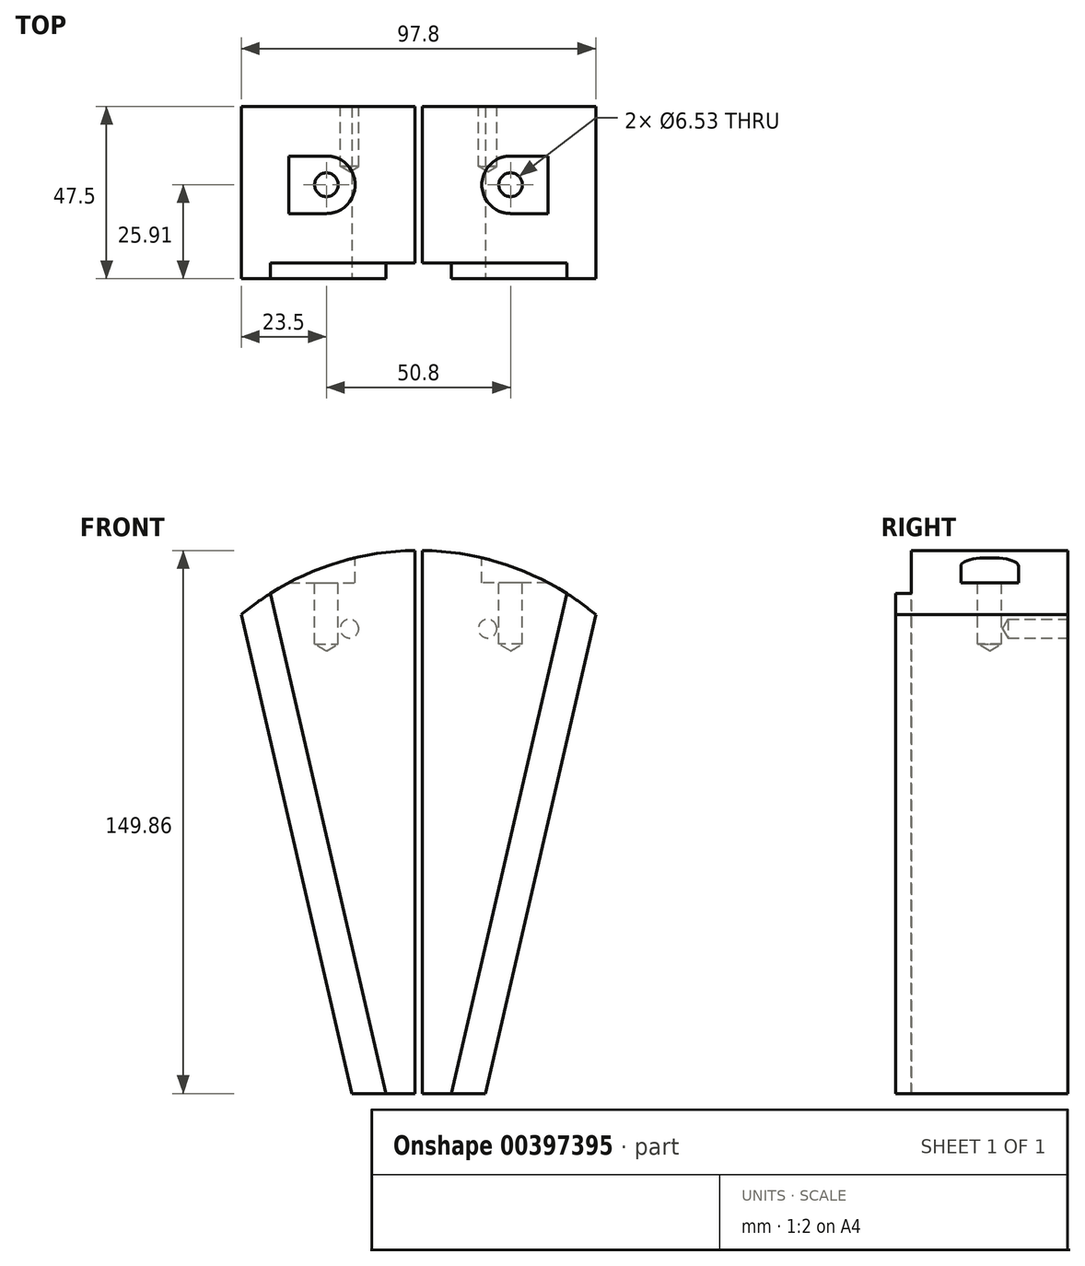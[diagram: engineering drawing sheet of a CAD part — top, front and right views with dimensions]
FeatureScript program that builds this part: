
annotation { "Feature Type Name" : "Feature", "Feature Type Description" : "" }
export const myFeature = defineFeature(function(context is Context, id is Id, definition is map)
    precondition{}
    {
        {
            var Q0;
            Q0=qCreatedBy(makeId("Front.planeOp"),FACE);
            var sketch = newSketch(context, id + "F0", { "sketchPlane" : qUnion([Q0])});
            skLineSegment(sketch, "E0", {"start": v(1.02, 76.2) * mm, "end": v(1.02, -73.67) * mm});
            skLineSegment(sketch, "E1", {"start": v(1.02, -73.67) * mm, "end": v(18.4, -73.67) * mm});
            skLineSegment(sketch, "E2", {"start": v(18.4, -73.67) * mm, "end": v(48.9, 58.44) * mm});
            skLineSegment(sketch, "E3", {"start": v(0, 78.33) * mm, "end": v(0, -85.86) * mm, "construction": true});
            skArc(sketch, "E4", {"start": v(48.9, 58.44) * mm, "mid": v(26, 71.62) * mm, "end": v(0, 76.2) * mm});
            skSolve(sketch);
        }
        {
            var Q0;
            {var subQ0=sQuery(id+"F0.wireOp",EDGE,"E0");Q0=makeQuery(id+"F0.imprint","IMPRINT",FACE,{"disambiguationData":[TD([[makeQuery(id+"F0.imprint","IMPRINT",EDGE,{"derivedFrom":subQ0}),1.0]])]});}
            extrude(context, id + "F1", {"entities" : qUnion([Q0]), "oppositeDirection" : true, "depth" : 21.59 * mm, "offsetDistance" : 25.4 * mm, "hasSecondDirection" : true, "secondDirectionOppositeDirection" : false, "secondDirectionDepth" : 25.9 * mm});
        }
        {
            var Q0;
            Q0=makeQuery(id+"F1.opExtrude","CAP_FACE",FACE,{"disambiguationData":[OSD([sQuery(id+"F0.wireOp",EDGE,"E0"),sQuery(id+"F0.wireOp",EDGE,"E1"),sQuery(id+"F0.wireOp",EDGE,"E2"),sQuery(id+"F0.wireOp",EDGE,"E4")])],"isStart":true});
            var sketch = newSketch(context, id + "F2", { "sketchPlane" : qUnion([Q0])});
            skLineSegment(sketch, "E5", {"start": v(9.01, -73.67) * mm, "end": v(40.87, 64.32) * mm});
            skSolve(sketch);
        }
        {
            var Q0;
            {var subQ0=sQuery(id+"F2.wireOp",EDGE,"E5");Q0=makeQuery(id+"F2.imprint","IMPRINT",FACE,{"disambiguationData":[TD([[makeQuery(id+"F2.imprint","IMPRINT",EDGE,{"derivedFrom":subQ0}),1.0]])]});}
            extrude(context, id + "F3", {"entities" : qUnion([Q0]), "operationType" : NewBodyOperationType.REMOVE, "oppositeDirection" : true, "depth" : 4.32 * mm, "offsetDistance" : 25.4 * mm});
        }
        {
            var Q0;
            Q0=qCreatedBy(makeId("Top.planeOp"),FACE);
            cPlane(context, id + "F4", {"entities" : qUnion([Q0]), "cplaneType" : CPlaneType.OFFSET, "offset" : 76.2 * mm, "width" : 152.4 * mm, "height" : 152.4 * mm});
        }
        {
            var Q0;
            Q0=qCreatedBy(id+"F4.planeOp",FACE);
            var sketch = newSketch(context, id + "F5", { "sketchPlane" : qUnion([Q0])});
            skLineSegment(sketch, "E6", {"start": v(35.75, 7.94) * mm, "end": v(35.75, -7.94) * mm});
            skLineSegment(sketch, "E7", {"start": v(35.75, -7.94) * mm, "end": v(25.4, -7.94) * mm});
            skLineSegment(sketch, "E8", {"start": v(35.75, 7.94) * mm, "end": v(25.4, 7.94) * mm});
            skArc(sketch, "E9", {"start": v(25.4, 7.94) * mm, "mid": v(17.46, 0) * mm, "end": v(25.4, -7.94) * mm});
            skSolve(sketch);
        }
        {
            var Q0;
            Q0=makeQuery(id+"F5.imprint","IMPRINT",FACE,{"disambiguationData":[TD([[makeQuery(id+"F5.imprint","IMPRINT",EDGE,{"derivedFrom":sQuery(id+"F5.wireOp",EDGE,"E6")}),-1.0]])]});
            extrude(context, id + "F6", {"entities" : qUnion([Q0]), "operationType" : NewBodyOperationType.REMOVE, "oppositeDirection" : true, "depth" : 8.9 * mm, "offsetDistance" : 25.4 * mm});
        }
        {
            var Q0;
            Q0=makeQuery(id+"F6.boolean.opBoolean","COPY",FACE,{"derivedFrom":makeQuery(id+"F6.opExtrude","CAP_FACE",FACE,{"disambiguationData":[OSD([sQuery(id+"F5.wireOp",EDGE,"E6"),sQuery(id+"F5.wireOp",EDGE,"E7"),sQuery(id+"F5.wireOp",EDGE,"E8"),sQuery(id+"F5.wireOp",EDGE,"E9")])],"isStart":false})});
            var sketch = newSketch(context, id + "F7", { "sketchPlane" : qUnion([Q0])});
            skCircle(sketch, "E10", {"center": v(25.4, 0) * mm, "radius": 3.26 * mm});
            skSolve(sketch);
        }
        {
            var Q0;
            Q0=sQuery(id+"F7.wireOp",VERTEX,"E10.center");
            var Q1;
            Q1=makeQuery(id+"F1.opExtrude","SWEPT_BODY",BODY,{"disambiguationData":[OSD([sQuery(id+"F0.wireOp",EDGE,"E0"),sQuery(id+"F0.wireOp",EDGE,"E1"),sQuery(id+"F0.wireOp",EDGE,"E2"),sQuery(id+"F0.wireOp",EDGE,"E4")])]});
            hole(context, id + "F8", {"style" : HoleStyle.SIMPLE, "endStyle" : HoleEndStyle.BLIND, "standardTappedOrClearance" : lookupTablePath({ "standard" : "ANSI", "engagement" : "75%", "pitch" : "18 tpi", "size" : "5/16", "type" : "Tapped" }), "standardBlindInLast" : lookupTablePath({ "standard" : "ANSI", "engagement" : "75%", "pitch" : "18 tpi", "size" : "5/16", "type" : "Tapped" }), "holeDiameter" : 6.53 * mm, "majorDiameter" : 7.94 * mm, "showTappedDepth" : true, "holeDepth" : 16.93 * mm, "isTappedThrough" : true, "tappedDepth" : 12.7 * mm, "tapClearance" : 3, "locations" : qUnion([Q0]), "scope" : qUnion([Q1])});
        }
        {
            var Q0;
            Q0=makeQuery(id+"F1.opExtrude","CAP_FACE",FACE,{"disambiguationData":[OSD([sQuery(id+"F0.wireOp",EDGE,"E0"),sQuery(id+"F0.wireOp",EDGE,"E1"),sQuery(id+"F0.wireOp",EDGE,"E2"),sQuery(id+"F0.wireOp",EDGE,"E4")])],"isStart":false});
            var sketch = newSketch(context, id + "F9", { "sketchPlane" : qUnion([Q0])});
            skCircle(sketch, "E11", {"center": v(-19.05, 54.6) * mm, "radius": 2.54 * mm});
            skSolve(sketch);
        }
        {
            var Q0;
            Q0=sQuery(id+"F9.wireOp",VERTEX,"E11.center");
            var Q1;
            Q1=makeQuery(id+"F1.opExtrude","SWEPT_BODY",BODY,{"disambiguationData":[OSD([sQuery(id+"F0.wireOp",EDGE,"E0"),sQuery(id+"F0.wireOp",EDGE,"E1"),sQuery(id+"F0.wireOp",EDGE,"E2"),sQuery(id+"F0.wireOp",EDGE,"E4")])]});
            hole(context, id + "F10", {"style" : HoleStyle.SIMPLE, "endStyle" : HoleEndStyle.BLIND, "standardTappedOrClearance" : lookupTablePath({ "standard" : "ANSI", "engagement" : "75%", "pitch" : "20 tpi", "size" : "1/4", "type" : "Tapped" }), "standardBlindInLast" : lookupTablePath({ "standard" : "ANSI", "engagement" : "75%", "pitch" : "20 tpi", "size" : "1/4", "type" : "Tapped" }), "holeDiameter" : 5.1 * mm, "majorDiameter" : 6.35 * mm, "showTappedDepth" : true, "holeDepth" : 16.52 * mm, "isTappedThrough" : true, "tappedDepth" : 12.7 * mm, "tapClearance" : 3, "locations" : qUnion([Q0]), "scope" : qUnion([Q1])});
        }
        {
            var Q0;
            Q0=makeQuery(id+"F1.opExtrude","SWEPT_BODY",BODY,{"disambiguationData":[OSD([sQuery(id+"F0.wireOp",EDGE,"E0"),sQuery(id+"F0.wireOp",EDGE,"E1"),sQuery(id+"F0.wireOp",EDGE,"E2"),sQuery(id+"F0.wireOp",EDGE,"E4")])]});
            var Q1;
            Q1=qCreatedBy(makeId("Right.planeOp"),FACE);
            mirror(context, id + "F11", {"entities" : qUnion([Q0]), "mirrorPlane" : qUnion([Q1])});
        }
    });
